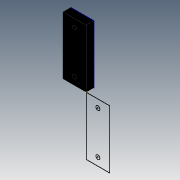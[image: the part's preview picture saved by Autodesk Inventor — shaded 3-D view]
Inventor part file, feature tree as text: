
AUTODESK INVENTOR PART (.ipt)
format: ipt  version: 2015 (Build 190159000, 159)  size: 92,672 bytes
history: native  units: mm
features: other x5, sketch x2, extrude x1, reference x1
ambient origin geometry x8: Origin, YZ Plane, XZ Plane, XY Plane, X Axis, Y Axis, Z Axis, Center Point
bodies: Body1 (feature_tree)
feature tree (9):
  other  "Blocks"
  extrude  "Extrusion2"  Depth=150.0mm
  sketch  "Sketch2"  dims[d4=10.0mm d5=10.0mm d6=20.0mm d7=20.0mm d8=30.0mm d9=20.0mm d10=0.0mm d11=30.0mm]
  other  "DXF"
  sketch  "Sketch1"  dims[d0=60.0mm d1=150.0mm]
  reference  "Reference1"
  other  "Block1"
  other  "Block1:1"
  other  "Block1:2"
